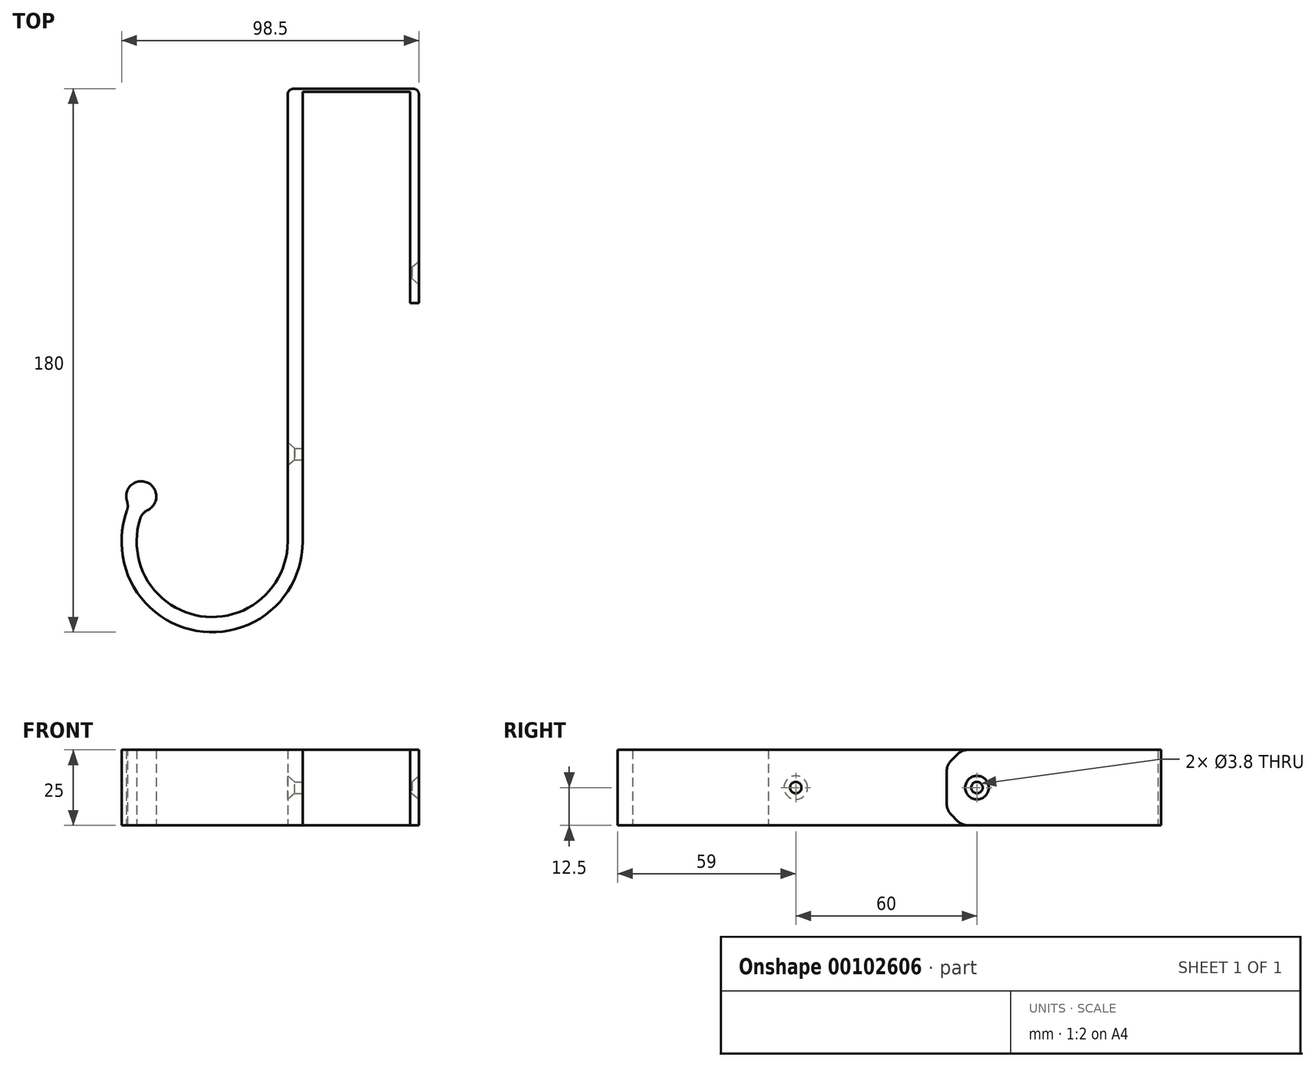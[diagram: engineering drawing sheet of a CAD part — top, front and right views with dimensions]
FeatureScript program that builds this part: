
annotation { "Feature Type Name" : "Feature", "Feature Type Description" : "" }
export const myFeature = defineFeature(function(context is Context, id is Id, definition is map)
    precondition{}
    {
        {
            var Q0;
            Q0=qCreatedBy(makeId("Top.planeOp"),FACE);
            var sketch = newSketch(context, id + "F0", { "sketchPlane" : qUnion([Q0])});
            skLineSegment(sketch, "E0", {"start": v(35.5, 0) * mm, "end": v(0, 0) * mm});
            skLineSegment(sketch, "E1", {"start": v(0, 0) * mm, "end": v(0, -149) * mm});
            skLineSegment(sketch, "E2", {"start": v(35.5, 0) * mm, "end": v(35.5, -70) * mm});
            skLineSegment(sketch, "E3", {"start": v(35.5, -70) * mm, "end": v(38.5, -70) * mm});
            skLineSegment(sketch, "E4", {"start": v(38.5, -70) * mm, "end": v(38.5, 1) * mm});
            skLineSegment(sketch, "E5", {"start": v(38.5, 1) * mm, "end": v(-5, 1) * mm});
            skLineSegment(sketch, "E6", {"start": v(-5, 1) * mm, "end": v(-5, -149) * mm});
            skArc(sketch, "E7", {"start": v(-52.91, -139) * mm, "mid": v(-35.1, -173.47) * mm, "end": v(-5, -149) * mm});
            skArc(sketch, "E8", {"start": v(-57.5, -137) * mm, "mid": v(-36.13, -178.37) * mm, "end": v(0, -149) * mm});
            skArc(sketch, "E9", {"start": v(-52.91, -139) * mm, "mid": v(-51.47, -129.45) * mm, "end": v(-57.5, -137) * mm});
            skLineSegment(sketch, "E10", {"start": v(-30, -149) * mm, "end": v(-57.5, -137) * mm, "construction": true});
            skSolve(sketch);
        }
        {
            var Q0;
            Q0 = qSketchRegion(id + "F0", true);
            extrude(context, id + "F1", {"entities" : qUnion([Q0]), "depth" : 25 * mm, "symmetric" : true});
        }
        {
            var Q0;
            Q0=makeQuery(id+"F1.opExtrude","CAP_EDGE",EDGE,{"disambiguationData":[OSD([sQuery(id+"F0.wireOp",EDGE,"E3")])],"isStart":false});
            var Q1;
            Q1=makeQuery(id+"F1.opExtrude","CAP_EDGE",EDGE,{"disambiguationData":[OSD([sQuery(id+"F0.wireOp",EDGE,"E3")])],"isStart":true});
            chamfer(context, id + "F2", {"entities" : qUnion([Q0, Q1]), "width" : 5 * mm, "tangentPropagation" : true});
        }
        {
            var Q0;
            Q0=makeQuery(id+"F1.opExtrude","SWEPT_EDGE",EDGE,{"disambiguationData":[OSD([sQuery(id+"F0.wireOp",EDGE,"E5"),sQuery(id+"F0.wireOp",EDGE,"E6")])]});
            var Q1;
            Q1=makeQuery(id+"F1.opExtrude","SWEPT_EDGE",EDGE,{"disambiguationData":[OSD([sQuery(id+"F0.wireOp",EDGE,"E4"),sQuery(id+"F0.wireOp",EDGE,"E5")])]});
            fillet(context, id + "F3", {"entities" : qUnion([Q0, Q1]), "radius" : 2 * mm, "tangentPropagation" : true, "allowEdgeOverflow" : false});
        }
        {
            var Q0;
            {var subQ0=sQuery(id+"F0.wireOp",EDGE,"E3");Q0=makeQuery(id+"F2.opChamfer","BLEND_EDGE",EDGE,{"blendedFrom":[makeQuery(id+"F1.opExtrude","CAP_EDGE",EDGE,{"disambiguationData":[OSD([subQ0])],"isStart":false}),makeQuery(id+"F1.opExtrude","CAP_FACE",FACE,{"disambiguationData":[OSD([sQuery(id+"F0.wireOp",EDGE,"E0"),sQuery(id+"F0.wireOp",EDGE,"E1"),sQuery(id+"F0.wireOp",EDGE,"E2"),subQ0,sQuery(id+"F0.wireOp",EDGE,"E4"),sQuery(id+"F0.wireOp",EDGE,"E5"),sQuery(id+"F0.wireOp",EDGE,"E6"),sQuery(id+"F0.wireOp",EDGE,"E7"),sQuery(id+"F0.wireOp",EDGE,"E8"),sQuery(id+"F0.wireOp",EDGE,"1F7OpqzS-G1bj-Dlt0-yZIZ-3sq5KjLCDXfu")])],"isStart":false})],"blendedInto":[makeQuery(id+"F1.opExtrude","CAP_FACE",FACE,{"disambiguationData":[OSD([sQuery(id+"F0.wireOp",EDGE,"E0"),sQuery(id+"F0.wireOp",EDGE,"E1"),sQuery(id+"F0.wireOp",EDGE,"E2"),subQ0,sQuery(id+"F0.wireOp",EDGE,"E4"),sQuery(id+"F0.wireOp",EDGE,"E5"),sQuery(id+"F0.wireOp",EDGE,"E6"),sQuery(id+"F0.wireOp",EDGE,"E7"),sQuery(id+"F0.wireOp",EDGE,"E8"),sQuery(id+"F0.wireOp",EDGE,"1F7OpqzS-G1bj-Dlt0-yZIZ-3sq5KjLCDXfu")])],"isStart":false})]});}
            var Q1;
            {var subQ0=sQuery(id+"F0.wireOp",EDGE,"E3");Q1=makeQuery(id+"F2.opChamfer","BLEND_EDGE",EDGE,{"blendedFrom":[makeQuery(id+"F1.opExtrude","CAP_EDGE",EDGE,{"disambiguationData":[OSD([subQ0])],"isStart":false}),makeQuery(id+"F1.opExtrude","SWEPT_FACE",FACE,{"disambiguationData":[OSD([subQ0])]})],"blendedInto":[makeQuery(id+"F1.opExtrude","SWEPT_FACE",FACE,{"disambiguationData":[OSD([subQ0])]})]});}
            var Q2;
            {var subQ0=sQuery(id+"F0.wireOp",EDGE,"E3");Q2=makeQuery(id+"F2.opChamfer","BLEND_EDGE",EDGE,{"blendedFrom":[makeQuery(id+"F1.opExtrude","CAP_EDGE",EDGE,{"disambiguationData":[OSD([subQ0])],"isStart":true}),makeQuery(id+"F1.opExtrude","CAP_FACE",FACE,{"disambiguationData":[OSD([sQuery(id+"F0.wireOp",EDGE,"E0"),sQuery(id+"F0.wireOp",EDGE,"E1"),sQuery(id+"F0.wireOp",EDGE,"E2"),subQ0,sQuery(id+"F0.wireOp",EDGE,"E4"),sQuery(id+"F0.wireOp",EDGE,"E5"),sQuery(id+"F0.wireOp",EDGE,"E6"),sQuery(id+"F0.wireOp",EDGE,"E7"),sQuery(id+"F0.wireOp",EDGE,"E8"),sQuery(id+"F0.wireOp",EDGE,"1F7OpqzS-G1bj-Dlt0-yZIZ-3sq5KjLCDXfu")])],"isStart":true})],"blendedInto":[makeQuery(id+"F1.opExtrude","CAP_FACE",FACE,{"disambiguationData":[OSD([sQuery(id+"F0.wireOp",EDGE,"E0"),sQuery(id+"F0.wireOp",EDGE,"E1"),sQuery(id+"F0.wireOp",EDGE,"E2"),subQ0,sQuery(id+"F0.wireOp",EDGE,"E4"),sQuery(id+"F0.wireOp",EDGE,"E5"),sQuery(id+"F0.wireOp",EDGE,"E6"),sQuery(id+"F0.wireOp",EDGE,"E7"),sQuery(id+"F0.wireOp",EDGE,"E8"),sQuery(id+"F0.wireOp",EDGE,"1F7OpqzS-G1bj-Dlt0-yZIZ-3sq5KjLCDXfu")])],"isStart":true})]});}
            var Q3;
            {var subQ0=sQuery(id+"F0.wireOp",EDGE,"E3");Q3=makeQuery(id+"F2.opChamfer","BLEND_EDGE",EDGE,{"blendedFrom":[makeQuery(id+"F1.opExtrude","CAP_EDGE",EDGE,{"disambiguationData":[OSD([subQ0])],"isStart":true}),makeQuery(id+"F1.opExtrude","SWEPT_FACE",FACE,{"disambiguationData":[OSD([subQ0])]})],"blendedInto":[makeQuery(id+"F1.opExtrude","SWEPT_FACE",FACE,{"disambiguationData":[OSD([subQ0])]})]});}
            fillet(context, id + "F4", {"entities" : qUnion([Q0, Q1, Q2, Q3]), "radius" : 5 * mm, "tangentPropagation" : true, "allowEdgeOverflow" : false});
        }
        {
            var Q0;
            Q0=makeQuery(id+"F1.opExtrude","SWEPT_FACE",FACE,{"disambiguationData":[OSD([sQuery(id+"F0.wireOp",EDGE,"E6")])]});
            var sketch = newSketch(context, id + "F5", { "sketchPlane" : qUnion([Q0])});
            skPoint(sketch, "E11", {"position": v(120, 0) * mm});
            skLineSegment(sketch, "E12", {"start": v(117.88, 0) * mm, "end": v(120, -2.12) * mm});
            skLineSegment(sketch, "E13", {"start": v(120, -2.12) * mm, "end": v(122.12, 0) * mm});
            skLineSegment(sketch, "E14", {"start": v(122.12, 0) * mm, "end": v(120, 2.12) * mm});
            skLineSegment(sketch, "E15", {"start": v(120, 2.12) * mm, "end": v(117.88, 0) * mm});
            skSolve(sketch);
        }
        {
            var Q0;
            Q0=makeQuery(id+"F1.opExtrude","SWEPT_EDGE",EDGE,{"disambiguationData":[OSD([sQuery(id+"F0.wireOp",EDGE,"E8"),sQuery(id+"F0.wireOp",EDGE,"E9")])]});
            var Q1;
            Q1=makeQuery(id+"F1.opExtrude","SWEPT_EDGE",EDGE,{"disambiguationData":[OSD([sQuery(id+"F0.wireOp",EDGE,"E7"),sQuery(id+"F0.wireOp",EDGE,"E9")])]});
            fillet(context, id + "F6", {"entities" : qUnion([Q0, Q1]), "radius" : 5 * mm, "tangentPropagation" : true, "allowEdgeOverflow" : false});
        }
        {
            var Q0;
            Q0=makeQuery(id+"F1.opExtrude","SWEPT_FACE",FACE,{"disambiguationData":[OSD([sQuery(id+"F0.wireOp",EDGE,"E4")])]});
            var sketch = newSketch(context, id + "F7", { "sketchPlane" : qUnion([Q0])});
            skPoint(sketch, "E16", {"position": v(-60, 0) * mm});
            skSolve(sketch);
        }
        {
            var Q0;
            Q0=sQuery(id+"F5.wireOp",VERTEX,"E11");
            var Q1;
            Q1=sQuery(id+"F7.wireOp",VERTEX,"E16");
            var Q2;
            Q2=makeQuery(id+"F1.opExtrude","SWEPT_BODY",BODY,{"disambiguationData":[OSD([sQuery(id+"F0.wireOp",EDGE,"E0"),sQuery(id+"F0.wireOp",EDGE,"E1"),sQuery(id+"F0.wireOp",EDGE,"E2"),sQuery(id+"F0.wireOp",EDGE,"E3"),sQuery(id+"F0.wireOp",EDGE,"E4"),sQuery(id+"F0.wireOp",EDGE,"E5"),sQuery(id+"F0.wireOp",EDGE,"E6"),sQuery(id+"F0.wireOp",EDGE,"E7"),sQuery(id+"F0.wireOp",EDGE,"E8"),sQuery(id+"F0.wireOp",EDGE,"1F7OpqzS-G1bj-Dlt0-yZIZ-3sq5KjLCDXfu")])]});
            hole(context, id + "F8", {"style" : HoleStyle.C_SINK, "endStyle" : HoleEndStyle.BLIND, "standardTappedOrClearance" : lookupTablePath({ "standard" : "ANSI", "fit" : "Normal (ASME)", "size" : "#6", "type" : "Clearance" }), "standardBlindInLast" : lookupTablePath({ "fit" : "Free", "standard" : "ANSI", "size" : "#6", "type" : "Clearance" }), "holeDiameter" : 3.8 * mm, "cSinkDiameter" : 7.8 * mm, "cSinkAngle" : 82 * degree, "holeDepth" : 5 * mm + 7.62 * mm, "locations" : qUnion([Q0, Q1]), "scope" : qUnion([Q2]), "startStyle" : HoleStartStyle.PART});
        }
    });
